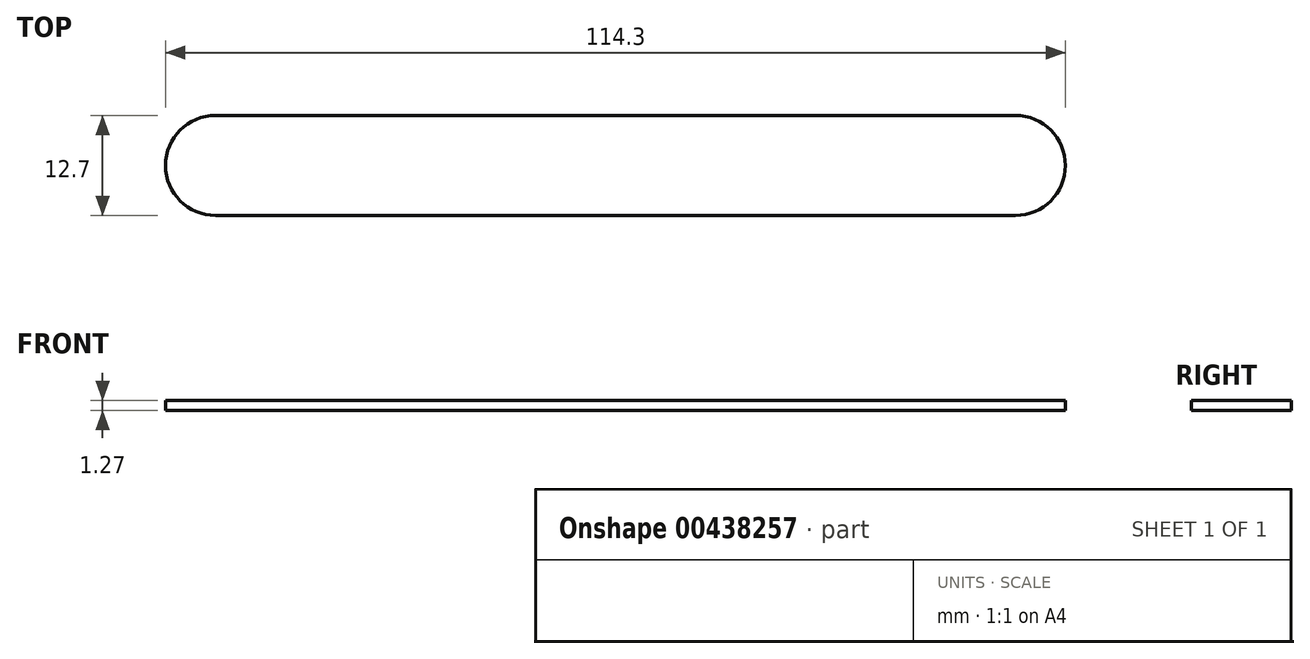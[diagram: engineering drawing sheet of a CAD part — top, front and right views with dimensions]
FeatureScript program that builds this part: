
annotation { "Feature Type Name" : "Feature", "Feature Type Description" : "" }
export const myFeature = defineFeature(function(context is Context, id is Id, definition is map)
    precondition{}
    {
        {
            var Q0;
            Q0=qCreatedBy(makeId("Top.planeOp"),FACE);
            var sketch = newSketch(context, id + "F0", { "sketchPlane" : qUnion([Q0])});
            skLineSegment(sketch, "E0.bottom", {"start": v(-56.14, 20.39) * mm, "end": v(45.46, 20.39) * mm});
            skLineSegment(sketch, "E0.top", {"start": v(-56.14, 7.69) * mm, "end": v(45.46, 7.69) * mm});
            skArc(sketch, "E1", {"start": v(-56.14, 20.39) * mm, "mid": v(-62.5, 14.04) * mm, "end": v(-56.14, 7.69) * mm});
            skArc(sketch, "E2", {"start": v(45.46, 7.69) * mm, "mid": v(51.8, 14.04) * mm, "end": v(45.46, 20.39) * mm});
            skSolve(sketch);
        }
        {
            var Q0;
            Q0 = qSketchRegion(id + "F0", true);
            extrude(context, id + "F1", {"entities" : qUnion([Q0]), "depth" : 1.27 * mm});
        }
    });
